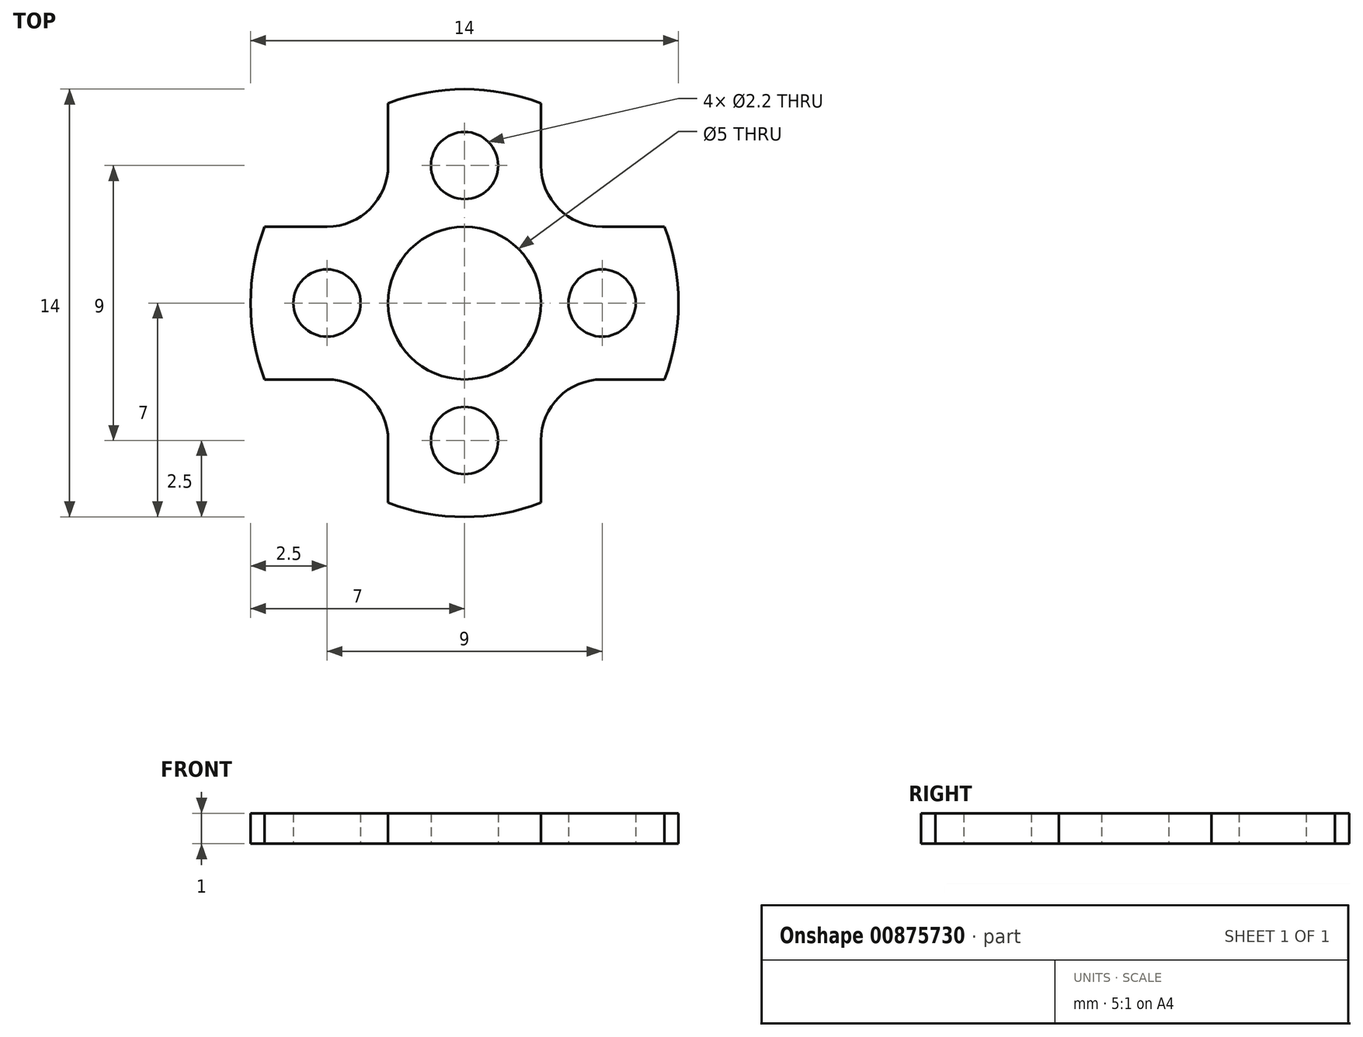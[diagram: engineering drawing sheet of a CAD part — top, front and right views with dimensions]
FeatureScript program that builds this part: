
annotation { "Feature Type Name" : "Feature", "Feature Type Description" : "" }
export const myFeature = defineFeature(function(context is Context, id is Id, definition is map)
    precondition{}
    {
        {
            var Q0;
            Q0=qCreatedBy(makeId("Top.planeOp"),FACE);
            var sketch = newSketch(context, id + "F0", { "sketchPlane" : qUnion([Q0])});
            skArc(sketch, "E0", {"start": v(2.5, 6.54) * mm, "mid": v(0, 7) * mm, "end": v(-2.5, 6.54) * mm});
            skPoint(sketch, "E1", {"position": v(4.5, 4.5) * mm});
            skCircle(sketch, "E2", {"center": v(0, 4.5) * mm, "radius": 1.1 * mm});
            skCircle(sketch, "E3", {"center": v(-4.5, 0) * mm, "radius": 1.1 * mm});
            skCircle(sketch, "E4", {"center": v(0, -4.5) * mm, "radius": 1.1 * mm});
            skCircle(sketch, "E5", {"center": v(4.5, 0) * mm, "radius": 1.1 * mm});
            skArc(sketch, "E6", {"start": v(2.5, 4.5) * mm, "mid": v(3.09, 3.09) * mm, "end": v(4.5, 2.5) * mm});
            skLineSegment(sketch, "E7", {"start": v(2.5, 4.5) * mm, "end": v(2.5, 6.54) * mm});
            skLineSegment(sketch, "E8", {"start": v(4.5, 2.5) * mm, "end": v(6.54, 2.5) * mm});
            skCircle(sketch, "E9", {"center": v(0, 0) * mm, "radius": 2.5 * mm});
            skArc(sketch, "E10", {"start": v(-4.5, 2.5) * mm, "mid": v(-3.09, 3.09) * mm, "end": v(-2.5, 4.5) * mm});
            skArc(sketch, "E11", {"start": v(-2.5, -4.5) * mm, "mid": v(-3.09, -3.09) * mm, "end": v(-4.5, -2.5) * mm});
            skArc(sketch, "E12", {"start": v(4.5, -2.5) * mm, "mid": v(3.09, -3.09) * mm, "end": v(2.5, -4.5) * mm});
            skLineSegment(sketch, "E13", {"start": v(-4.5, 2.5) * mm, "end": v(-6.54, 2.5) * mm});
            skLineSegment(sketch, "E14", {"start": v(-2.5, 4.5) * mm, "end": v(-2.5, 6.54) * mm});
            skLineSegment(sketch, "E15", {"start": v(-2.5, -4.5) * mm, "end": v(-2.5, -6.54) * mm});
            skLineSegment(sketch, "E16", {"start": v(-4.5, -2.5) * mm, "end": v(-6.54, -2.5) * mm});
            skLineSegment(sketch, "E17", {"start": v(2.5, -4.5) * mm, "end": v(2.5, -6.54) * mm});
            skLineSegment(sketch, "E18", {"start": v(4.5, -2.5) * mm, "end": v(6.54, -2.5) * mm});
            skArc(sketch, "E19.trimOffspring", {"start": v(-6.54, 2.5) * mm, "mid": v(-7, 0) * mm, "end": v(-6.54, -2.5) * mm});
            skArc(sketch, "E20.trimOffspring", {"start": v(6.54, -2.5) * mm, "mid": v(7, 0) * mm, "end": v(6.54, 2.5) * mm});
            skArc(sketch, "E21.trimOffspring", {"start": v(-2.5, -6.54) * mm, "mid": v(0, -7) * mm, "end": v(2.5, -6.54) * mm});
            skSolve(sketch);
        }
        {
            var Q0;
            Q0=makeQuery(id+"F0.imprint","IMPRINT",FACE,{"disambiguationData":[TD([[makeQuery(id+"F0.imprint","IMPRINT",EDGE,{"derivedFrom":sQuery(id+"F0.wireOp",EDGE,"E0")}),1.0]])]});
            extrude(context, id + "F1", {"entities" : qUnion([Q0]), "flatOperationType" : FlatOperationType.REMOVE, "depth" : 1 * mm, "offsetDistance" : 25 * mm, "domain" : OperationDomain.MODEL});
        }
    });
